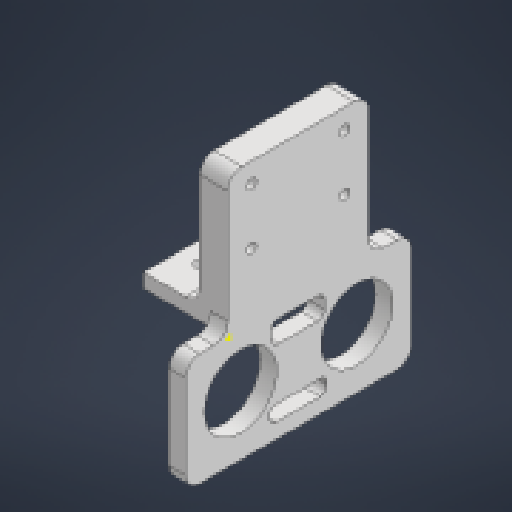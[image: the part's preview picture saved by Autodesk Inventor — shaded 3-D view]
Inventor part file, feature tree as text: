
AUTODESK INVENTOR PART (.ipt)
format: ipt  version: 2023 (Build 270158000, 158)  size: 241,152 bytes
history: native  units: in
note: dims shown in document units (in); Inventor stores cm internally (conversion verified against a paired STEP export)
features: reference x22, sketch x10, extrude x7, other x4, fillet x3, hole x2, projected_geometry x1
ambient origin geometry x8: Origin, YZ Plane, XZ Plane, XY Plane, X Axis, Y Axis, Z Axis, Center Point
bodies: Solid1 (feature_tree)
feature tree (49):
  extrude  "Extrusion1"  Depth=1.25in
  extrude  "Extrusion3"  Depth=0.5in
  fillet  "Fillet1"  Radius=0.125in
  fillet  "Fillet2"  Radius=0.125in
  hole  "Hole1"  [1 undecoded]
  extrude  "Extrusion4"  Depth=2.0in
  hole  "Hole2"  [1 undecoded]
  extrude  "Extrusion6"  Depth=0.5in TaperAngle=0.0deg
  fillet  "Fillet3"  Radius=0.15in
  extrude  "Extrusion11"  Depth=0.15in TaperAngle=0.0deg
  extrude  "Extrusion13"  Depth=0.006in
  sketch  "Sketch15"  dims[d60=0.006in d61=0.006in]
  extrude  "Extrusion14"  Depth=1.0in
  sketch  "Sketch1"  dims[d0=1.25in d1=1.25in]
  sketch  "Sketch3"  dims[d2=0.25in d3=0.0in d10=0.5in d11=0.125in d12=0.0in d13=0.125in]
  sketch  "Sketch4"  dims[d14=0.125in d15=0.1875in]
  projected_geometry  "Projected Loop2"
  sketch  "Sketch5"  dims[d17=0.3125in]
  sketch  "Sketch6"  dims[d18=0.0945in d19=0.75in d20=0.375in d21=0.25in d22=0.5635in d23=1.0in d24=0.8108in d25=2.0in]
  reference  "Reference1"
  reference  "Reference2"
  reference  "Reference3"
  reference  "Reference4"
  sketch  "Sketch7"  dims[d26=0.375in d27=1.0in d28=0.0in]
  reference  "Reference5"
  reference  "Reference6"
  reference  "Reference7"
  reference  "Reference8"
  reference  "Reference9"
  reference  "Reference10"
  reference  "Reference11"
  reference  "Reference12"
  reference  "Reference13"
  reference  "Reference14"
  reference  "Reference15"
  reference  "Reference16"
  reference  "Reference17"
  reference  "Reference18"
  reference  "Reference19"
  reference  "Reference20"
  reference  "Reference21"
  reference  "Reference22"
  sketch  "Sketch12"  dims[d31=0.0866in d32=0.75in d33=0.375in d34=0.25in d35=0.5635in d36=1.0in d37=0.8108in d38=0.5in d39=0.0in d40=0.15in]
  sketch  "Sketch14"  dims[d41=0.125in d54=0.15in d55=0.0in]
  sketch  "Sketch16"  dims[d62=1.0in d63=0.0in d64=0.005in d65=0.3446in d66=1.0in d67=0.0in]
  other  "<userpath>\Documents\GitHub\SDP-Kepler-1708b\FlyingUGV.iam"
  other  "FlyingUGV.iam"
  other  "Cam V2.1 v1:1"
  other  "soporte:1"
note: 2 required parameter values undecoded (feature->parameter linkage not recoverable at this tier; creation-order binding heuristic only, values carry confidence <= 0.55)
